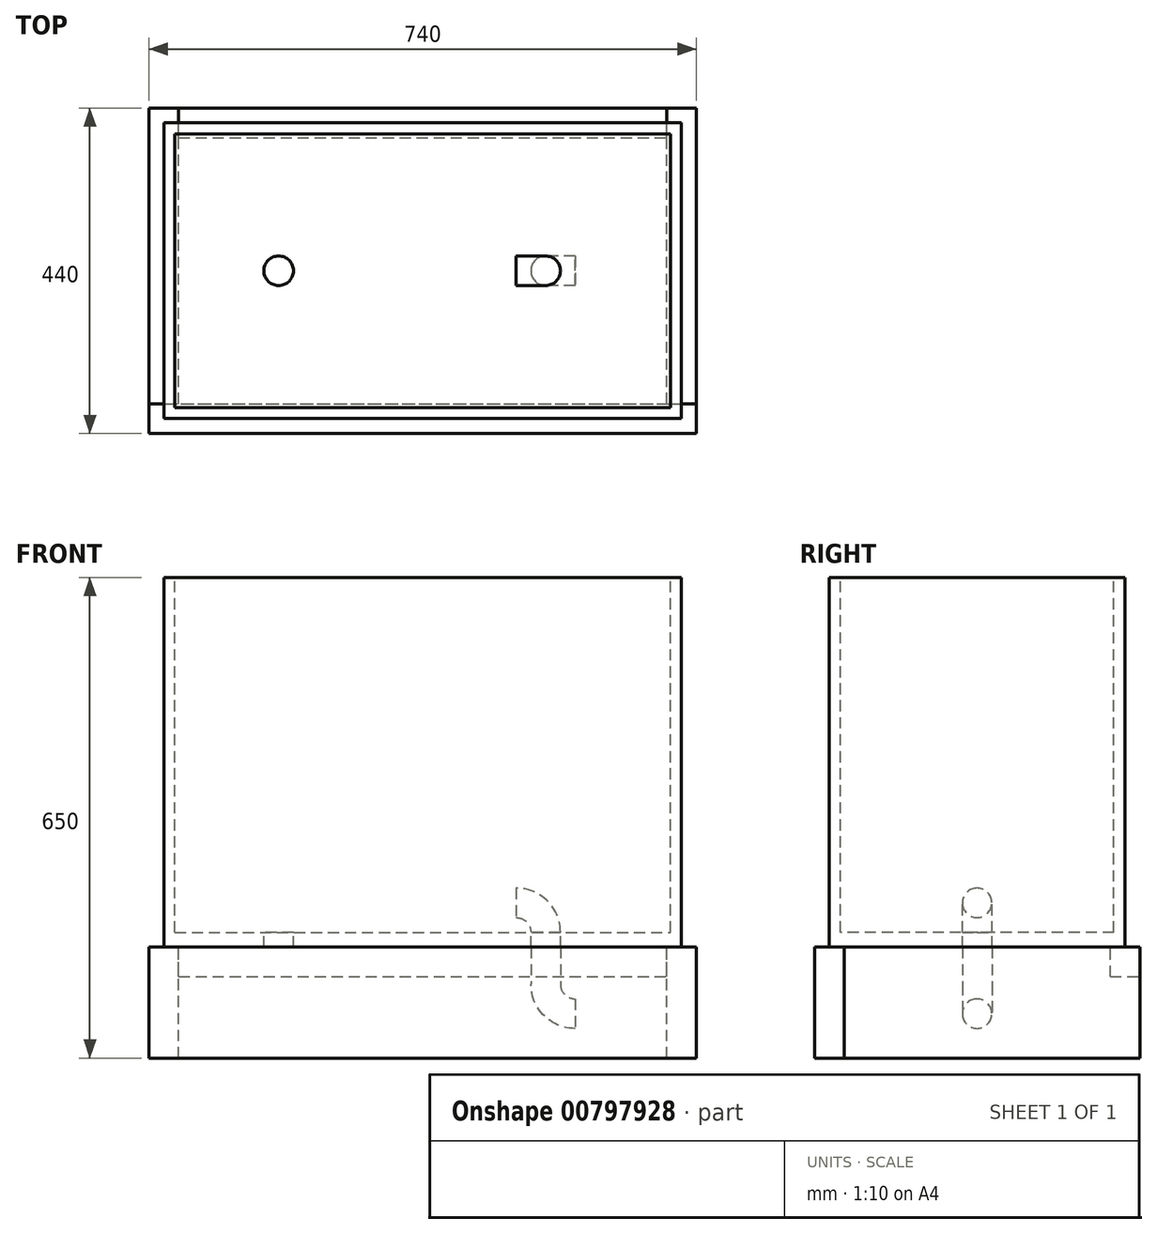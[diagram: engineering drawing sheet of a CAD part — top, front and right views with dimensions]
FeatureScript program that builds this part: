
annotation { "Feature Type Name" : "Feature", "Feature Type Description" : "" }
export const myFeature = defineFeature(function(context is Context, id is Id, definition is map)
    precondition{}
    {
        {
            var Q0;
            Q0=qCreatedBy(makeId("Top.planeOp"),FACE);
            var sketch = newSketch(context, id + "F0", { "sketchPlane" : qUnion([Q0])});
            skLineSegment(sketch, "E0.bottom", {"start": v(-360.5, 167.36) * mm, "end": v(339.5, 167.36) * mm});
            skLineSegment(sketch, "E0.top", {"start": v(-360.5, -232.64) * mm, "end": v(339.5, -232.64) * mm});
            skLineSegment(sketch, "E0.left", {"start": v(-360.5, 167.36) * mm, "end": v(-360.5, -232.64) * mm});
            skLineSegment(sketch, "E0.right", {"start": v(339.5, 167.36) * mm, "end": v(339.5, -232.64) * mm});
            skSolve(sketch);
        }
        {
            var Q0;
            Q0=makeQuery(id+"F0.imprint","IMPRINT",FACE,{"disambiguationData":[TD([[makeQuery(id+"F0.imprint","IMPRINT",EDGE,{"derivedFrom":sQuery(id+"F0.wireOp",EDGE,"E0.bottom")}),-1.0]])]});
            extrude(context, id + "F1", {"entities" : qUnion([Q0]), "depth" : 500 * mm, "offsetDistance" : 25 * mm});
        }
        {
            var Q0;
            Q0=makeQuery(id+"F1.opExtrude","CAP_FACE",FACE,{"disambiguationData":[OSD([sQuery(id+"F0.wireOp",EDGE,"E0.bottom"),sQuery(id+"F0.wireOp",EDGE,"E0.top"),sQuery(id+"F0.wireOp",EDGE,"E0.left"),sQuery(id+"F0.wireOp",EDGE,"E0.right")])],"isStart":false});
            var sketch = newSketch(context, id + "F2", { "sketchPlane" : qUnion([Q0])});
            skLineSegment(sketch, "E1.bottom", {"start": v(-345.5, 152.36) * mm, "end": v(324.5, 152.36) * mm});
            skLineSegment(sketch, "E1.top", {"start": v(-345.5, -217.64) * mm, "end": v(324.5, -217.64) * mm});
            skLineSegment(sketch, "E1.left", {"start": v(-345.5, 152.36) * mm, "end": v(-345.5, -217.64) * mm});
            skLineSegment(sketch, "E1.right", {"start": v(324.5, 152.36) * mm, "end": v(324.5, -217.64) * mm});
            skSolve(sketch);
        }
        {
            var Q0;
            Q0=makeQuery(id+"F2.imprint","IMPRINT",FACE,{"disambiguationData":[TD([[makeQuery(id+"F2.imprint","IMPRINT",EDGE,{"derivedFrom":sQuery(id+"F2.wireOp",EDGE,"E1.bottom")}),-1.0]])]});
            var Q1;
            Q1=makeQuery(id+"F1.opExtrude","CAP_FACE",FACE,{"disambiguationData":[OSD([sQuery(id+"F0.wireOp",EDGE,"E0.bottom"),sQuery(id+"F0.wireOp",EDGE,"E0.top"),sQuery(id+"F0.wireOp",EDGE,"E0.left"),sQuery(id+"F0.wireOp",EDGE,"E0.right")])],"isStart":true});
            extrude(context, id + "F3", {"entities" : qUnion([Q0]), "operationType" : NewBodyOperationType.REMOVE, "oppositeDirection" : true, "depth" : 480 * mm, "endBoundEntityFace" : qUnion([Q1]), "offsetDistance" : 25 * mm});
        }
        {
            var Q0;
            Q0=makeQuery(id+"F1.opExtrude","CAP_FACE",FACE,{"disambiguationData":[OSD([sQuery(id+"F0.wireOp",EDGE,"E0.bottom"),sQuery(id+"F0.wireOp",EDGE,"E0.top"),sQuery(id+"F0.wireOp",EDGE,"E0.left"),sQuery(id+"F0.wireOp",EDGE,"E0.right")])],"isStart":true});
            var sketch = newSketch(context, id + "F4", { "sketchPlane" : qUnion([Q0])});
            skLineSegment(sketch, "E2.bottom", {"start": v(-380.5, 252.64) * mm, "end": v(359.5, 252.64) * mm});
            skLineSegment(sketch, "E2.top", {"start": v(-380.5, 212.64) * mm, "end": v(359.5, 212.64) * mm});
            skLineSegment(sketch, "E2.left", {"start": v(-380.5, 252.64) * mm, "end": v(-380.5, 212.64) * mm});
            skLineSegment(sketch, "E2.right", {"start": v(359.5, 252.64) * mm, "end": v(359.5, 212.64) * mm});
            skLineSegment(sketch, "E3.bottom", {"start": v(-380.5, 212.64) * mm, "end": v(-340.5, 212.64) * mm});
            skLineSegment(sketch, "E3.top", {"start": v(-380.5, -187.36) * mm, "end": v(-340.5, -187.36) * mm});
            skLineSegment(sketch, "E3.left", {"start": v(-380.5, 212.64) * mm, "end": v(-380.5, -187.36) * mm});
            skLineSegment(sketch, "E3.right", {"start": v(-340.5, 212.64) * mm, "end": v(-340.5, -187.36) * mm});
            skLineSegment(sketch, "E4.bottom", {"start": v(359.5, 212.64) * mm, "end": v(319.5, 212.64) * mm});
            skLineSegment(sketch, "E4.top", {"start": v(359.5, -187.36) * mm, "end": v(319.5, -187.36) * mm});
            skLineSegment(sketch, "E4.left", {"start": v(359.5, 212.64) * mm, "end": v(359.5, -187.36) * mm});
            skLineSegment(sketch, "E4.right", {"start": v(319.5, 212.64) * mm, "end": v(319.5, -187.36) * mm});
            skLineSegment(sketch, "E5.bottom", {"start": v(-340.5, -187.36) * mm, "end": v(319.5, -187.36) * mm});
            skLineSegment(sketch, "E5.top", {"start": v(-340.5, -147.36) * mm, "end": v(319.5, -147.36) * mm});
            skLineSegment(sketch, "E5.left", {"start": v(-340.5, -187.36) * mm, "end": v(-340.5, -147.36) * mm});
            skLineSegment(sketch, "E5.right", {"start": v(319.5, -187.36) * mm, "end": v(319.5, -147.36) * mm});
            skSolve(sketch);
        }
        {
            var Q0;
            {var subQ1=sQuery(id+"F4.wireOp",EDGE,"E3.top");Q0=makeQuery(id+"F4.imprint","IMPRINT",FACE,{"disambiguationData":[TD([[makeQuery(id+"F4.imprint","IMPRINT",EDGE,{"derivedFrom":subQ1}),1.0]])]});}
            var Q1;
            {var subQ3=makeQuery(id+"F1.opExtrude","CAP_EDGE",EDGE,{"disambiguationData":[OSD([sQuery(id+"F0.wireOp",EDGE,"E0.left")])],"isStart":true});var subQ5=makeQuery(id+"F1.opExtrude","CAP_EDGE",EDGE,{"disambiguationData":[OSD([sQuery(id+"F0.wireOp",EDGE,"E0.bottom")])],"isStart":true});var subQ6=makeQuery(id+"F4.imprint","INTERSECT",VERTEX,{"derivedFrom":[subQ5,subQ3]});Q1=makeQuery(id+"F4.imprint","IMPRINT",FACE,{"disambiguationData":[TD([[makeQuery(id+"F4.imprint","IMPRINT",EDGE,{"disambiguationData":[TD([[subQ6,-1.0]])],"derivedFrom":subQ5}),1.0]])]});}
            extrude(context, id + "F5", {"entities" : qUnion([Q0, Q1]), "depth" : 150 * mm, "offsetDistance" : 25 * mm});
        }
        {
            var Q0;
            Q0=makeQuery(id+"F4.imprint","IMPRINT",FACE,{"disambiguationData":[TD([[makeQuery(id+"F4.imprint","IMPRINT",EDGE,{"derivedFrom":sQuery(id+"F4.wireOp",EDGE,"E2.bottom")}),-1.0]])]});
            var Q1;
            {var subQ1=sQuery(id+"F4.wireOp",EDGE,"E2.top");Q1=makeQuery(id+"F4.imprint","IMPRINT",FACE,{"disambiguationData":[TD([[makeQuery(id+"F4.imprint","IMPRINT",EDGE,{"derivedFrom":subQ1}),1.0]])]});}
            extrude(context, id + "F6", {"entities" : qUnion([Q0, Q1]), "depth" : 150 * mm, "offsetDistance" : 25 * mm});
        }
        {
            var Q0;
            {var subQ1=sQuery(id+"F4.wireOp",EDGE,"E4.top");Q0=makeQuery(id+"F4.imprint","IMPRINT",FACE,{"disambiguationData":[TD([[makeQuery(id+"F4.imprint","IMPRINT",EDGE,{"derivedFrom":subQ1}),-1.0]])]});}
            var Q1;
            {var subQ3=makeQuery(id+"F1.opExtrude","CAP_EDGE",EDGE,{"disambiguationData":[OSD([sQuery(id+"F0.wireOp",EDGE,"E0.right")])],"isStart":true});var subQ5=makeQuery(id+"F1.opExtrude","CAP_EDGE",EDGE,{"disambiguationData":[OSD([sQuery(id+"F0.wireOp",EDGE,"E0.bottom")])],"isStart":true});var subQ7=makeQuery(id+"F4.imprint","INTERSECT",VERTEX,{"derivedFrom":[subQ5,subQ3]});Q1=makeQuery(id+"F4.imprint","IMPRINT",FACE,{"disambiguationData":[TD([[makeQuery(id+"F4.imprint","IMPRINT",EDGE,{"disambiguationData":[TD([[subQ7,1.0]])],"derivedFrom":subQ5}),1.0]])]});}
            extrude(context, id + "F7", {"entities" : qUnion([Q0, Q1]), "depth" : 150 * mm, "offsetDistance" : 25 * mm});
        }
        {
            var Q0;
            {var subQ0=sQuery(id+"F4.wireOp",EDGE,"E5.bottom");Q0=makeQuery(id+"F4.imprint","IMPRINT",FACE,{"disambiguationData":[TD([[makeQuery(id+"F4.imprint","IMPRINT",EDGE,{"derivedFrom":subQ0}),1.0]])]});}
            var Q1;
            {var subQ0=sQuery(id+"F4.wireOp",EDGE,"E5.top");Q1=makeQuery(id+"F4.imprint","IMPRINT",FACE,{"disambiguationData":[TD([[makeQuery(id+"F4.imprint","IMPRINT",EDGE,{"derivedFrom":subQ0}),-1.0]])]});}
            extrude(context, id + "F8", {"entities" : qUnion([Q0, Q1]), "depth" : 40 * mm, "offsetDistance" : 25 * mm});
        }
        {
            var Q0;
            Q0=makeQuery(id+"F3.boolean.opBoolean","COPY",FACE,{"derivedFrom":makeQuery(id+"F3.opExtrude","CAP_FACE",FACE,{"disambiguationData":[OSD([sQuery(id+"F2.wireOp",EDGE,"E1.bottom"),sQuery(id+"F2.wireOp",EDGE,"E1.top"),sQuery(id+"F2.wireOp",EDGE,"E1.left"),sQuery(id+"F2.wireOp",EDGE,"E1.right")])],"isStart":false})});
            var sketch = newSketch(context, id + "F9", { "sketchPlane" : qUnion([Q0])});
            skLineSegment(sketch, "E6", {"start": v(-345.5, -32.64) * mm, "end": v(324.5, -32.64) * mm, "construction": true});
            skCircle(sketch, "E7", {"center": v(-205.23, -32.64) * mm, "radius": 20 * mm});
            skCircle(sketch, "E8", {"center": v(155.95, -32.64) * mm, "radius": 20 * mm});
            skSolve(sketch);
        }
        {
            var Q0;
            Q0=makeQuery(id+"F9.imprint","IMPRINT",FACE,{"disambiguationData":[TD([[makeQuery(id+"F9.imprint","IMPRINT",EDGE,{"derivedFrom":sQuery(id+"F9.wireOp",EDGE,"E7")}),1.0]])]});
            var Q1;
            Q1=makeQuery(id+"F9.imprint","IMPRINT",FACE,{"disambiguationData":[TD([[makeQuery(id+"F9.imprint","IMPRINT",EDGE,{"derivedFrom":sQuery(id+"F9.wireOp",EDGE,"E8")}),1.0]])]});
            extrude(context, id + "F10", {"entities" : qUnion([Q0, Q1]), "operationType" : NewBodyOperationType.REMOVE, "endBound" : BoundingType.THROUGH_ALL, "oppositeDirection" : true, "depth" : 25 * mm, "offsetDistance" : 25 * mm});
        }
        {
            var Q0;
            Q0=makeQuery(id+"F3.boolean.opBoolean","COPY",FACE,{"derivedFrom":makeQuery(id+"F3.opExtrude","SWEPT_FACE",FACE,{"disambiguationData":[OSD([sQuery(id+"F2.wireOp",EDGE,"E1.bottom")])]})});
            var Q1;
            Q1=makeQuery(id+"F3.boolean.opBoolean","COPY",FACE,{"derivedFrom":makeQuery(id+"F3.opExtrude","SWEPT_FACE",FACE,{"disambiguationData":[OSD([sQuery(id+"F2.wireOp",EDGE,"E1.top")])]})});
            cPlane(context, id + "F11", {"entities" : qUnion([Q0, Q1]), "cplaneType" : CPlaneType.MID_PLANE, "offset" : 25 * mm, "width" : 150 * mm, "height" : 150 * mm});
        }
        {
            var Q0;
            Q0=qCreatedBy(id+"F11.planeOp",FACE);
            var sketch = newSketch(context, id + "F12", { "sketchPlane" : qUnion([Q0])});
            skArc(sketch, "E9", {"start": v(155.95, 20) * mm, "mid": v(144.24, 48.28) * mm, "end": v(115.95, 60) * mm});
            skLineSegment(sketch, "E10.0", {"start": v(-345.5, 20) * mm, "end": v(324.5, 20) * mm});
            skPoint(sketch, "E11.0", {"position": v(155.95, 20) * mm});
            skPoint(sketch, "E12.0", {"position": v(-205.23, 20) * mm});
            skLineSegment(sketch, "E13.0", {"start": v(-340.5, 0) * mm, "end": v(319.5, 0) * mm});
            skLineSegment(sketch, "E14", {"start": v(155.95, 20) * mm, "end": v(155.95, 0) * mm, "construction": true});
            skLineSegment(sketch, "E15", {"start": v(155.95, 0) * mm, "end": v(155.95, -50) * mm});
            skArc(sketch, "E16", {"start": v(195.95, -90) * mm, "mid": v(167.67, -78.28) * mm, "end": v(155.95, -50) * mm});
            skSolve(sketch);
        }
        {
            var Q0;
            Q0=makeQuery(id+"F9.imprint","IMPRINT",FACE,{"disambiguationData":[TD([[makeQuery(id+"F9.imprint","IMPRINT",EDGE,{"derivedFrom":sQuery(id+"F9.wireOp",EDGE,"E8")}),1.0]])]});
            var Q1;
            Q1=sQuery(id+"F12.wireOp",EDGE,"E9");
            sweep(context, id + "F13", {"profiles" : qUnion([Q0]), "path" : qUnion([Q1])});
        }
        {
            var Q0;
            Q0=makeQuery(id+"F1.opExtrude","CAP_FACE",FACE,{"disambiguationData":[OSD([sQuery(id+"F0.wireOp",EDGE,"E0.bottom"),sQuery(id+"F0.wireOp",EDGE,"E0.top"),sQuery(id+"F0.wireOp",EDGE,"E0.left"),sQuery(id+"F0.wireOp",EDGE,"E0.right")])],"isStart":true});
            var sketch = newSketch(context, id + "F14", { "sketchPlane" : qUnion([Q0])});
            skCircle(sketch, "E17.0.0", {"center": v(155.95, 32.64) * mm, "radius": 20 * mm});
            skSolve(sketch);
        }
        {
            var Q0;
            Q0=makeQuery(id+"F14.imprint","IMPRINT",FACE,{"disambiguationData":[TD([[makeQuery(id+"F14.imprint","IMPRINT",EDGE,{"derivedFrom":sQuery(id+"F14.wireOp",EDGE,"E17.0.0")}),-1.0]])]});
            var Q1;
            Q1=sQuery(id+"F12.wireOp",EDGE,"E15");
            var Q2;
            Q2=sQuery(id+"F12.wireOp",EDGE,"E16");
            sweep(context, id + "F15", {"profiles" : qUnion([Q0]), "path" : qUnion([Q1, Q2])});
        }
    });
